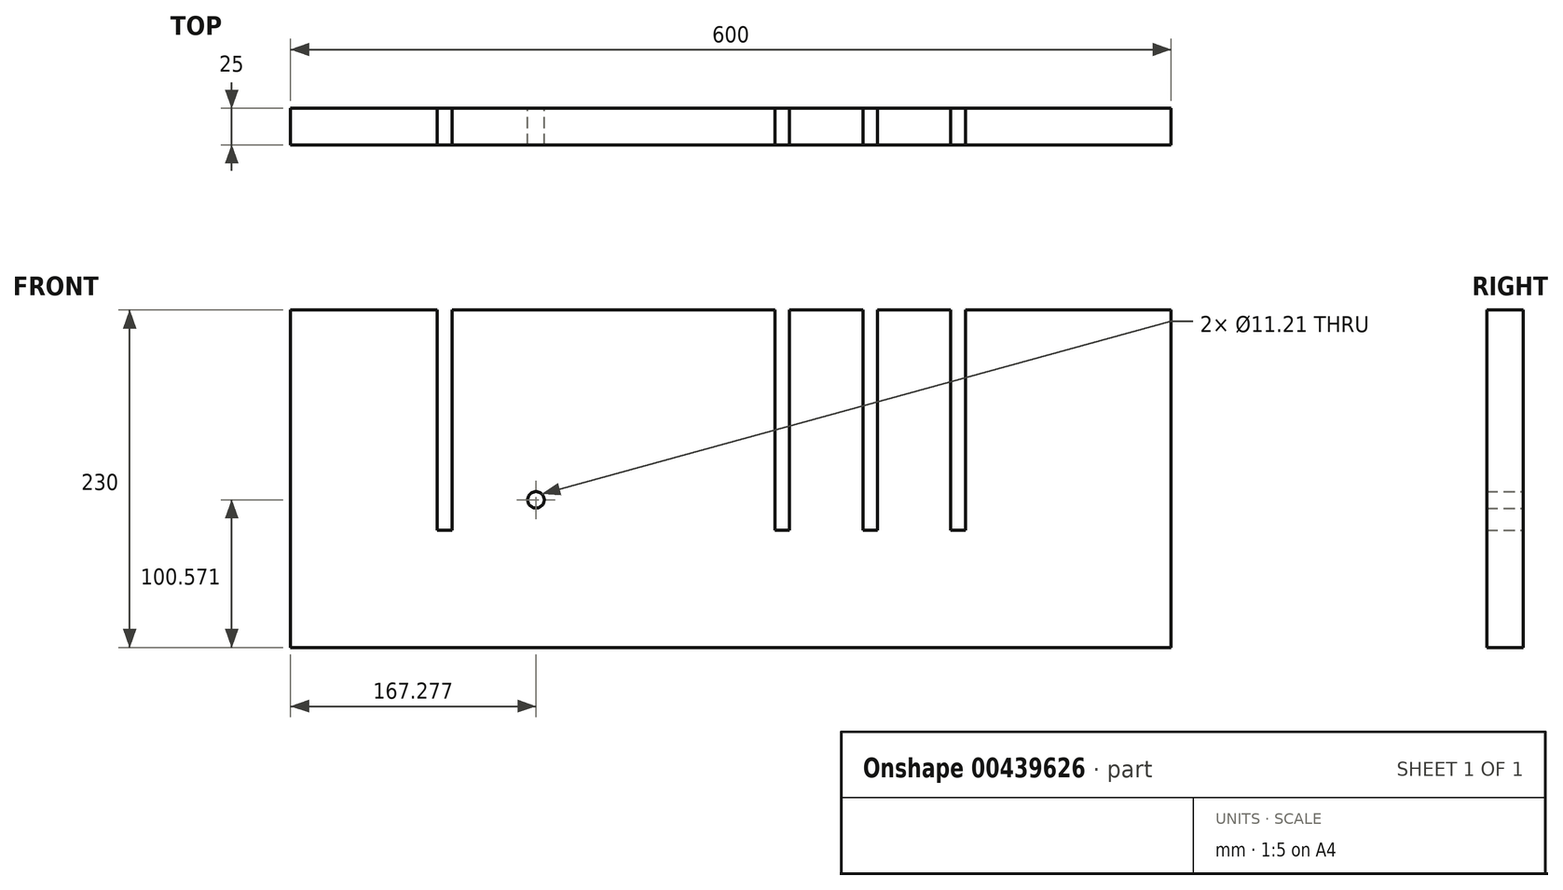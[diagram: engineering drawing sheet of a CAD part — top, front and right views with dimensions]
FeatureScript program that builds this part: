
annotation { "Feature Type Name" : "Feature", "Feature Type Description" : "" }
export const myFeature = defineFeature(function(context is Context, id is Id, definition is map)
    precondition{}
    {
        {
            var Q0;
            Q0=qCreatedBy(makeId("Front.planeOp"),FACE);
            var sketch = newSketch(context, id + "F0", { "sketchPlane" : qUnion([Q0])});
            skLineSegment(sketch, "E0.bottom", {"start": v(-153.84, 195.52) * mm, "end": v(-53.84, 195.52) * mm});
            skLineSegment(sketch, "E0.top", {"start": v(-153.84, -34.48) * mm, "end": v(446.16, -34.48) * mm});
            skLineSegment(sketch, "E0.left", {"start": v(-153.84, 195.52) * mm, "end": v(-153.84, -34.48) * mm});
            skLineSegment(sketch, "E0.right", {"start": v(446.16, 195.52) * mm, "end": v(446.16, -34.48) * mm});
            skLineSegment(sketch, "E1.0", {"start": v(-53.84, 195.52) * mm, "end": v(-53.84, 45.52) * mm});
            skLineSegment(sketch, "E2.0", {"start": v(-43.84, 195.52) * mm, "end": v(-43.84, 45.52) * mm});
            skLineSegment(sketch, "E3.0", {"start": v(176.16, 195.52) * mm, "end": v(176.16, 45.52) * mm});
            skLineSegment(sketch, "E4.0", {"start": v(186.16, 195.52) * mm, "end": v(186.16, 45.52) * mm});
            skLineSegment(sketch, "E5.0", {"start": v(236.16, 195.52) * mm, "end": v(236.16, 45.52) * mm});
            skLineSegment(sketch, "E6.0", {"start": v(246.16, 195.52) * mm, "end": v(246.16, 45.52) * mm});
            skLineSegment(sketch, "E7.0", {"start": v(296.16, 195.52) * mm, "end": v(296.16, 45.52) * mm});
            skLineSegment(sketch, "E8.0", {"start": v(306.16, 195.52) * mm, "end": v(306.16, 45.52) * mm});
            skLineSegment(sketch, "E9.0", {"start": v(-53.84, 45.52) * mm, "end": v(-43.84, 45.52) * mm});
            skLineSegment(sketch, "E10.trimOffspring", {"start": v(176.16, 45.52) * mm, "end": v(186.16, 45.52) * mm});
            skLineSegment(sketch, "E11.trimOffspring", {"start": v(296.16, 45.52) * mm, "end": v(306.16, 45.52) * mm});
            skLineSegment(sketch, "E12", {"start": v(236.16, 45.52) * mm, "end": v(246.16, 45.52) * mm});
            skLineSegment(sketch, "E13.trimOffspring", {"start": v(306.16, 195.52) * mm, "end": v(446.16, 195.52) * mm});
            skLineSegment(sketch, "E14.trimOffspring", {"start": v(246.16, 195.52) * mm, "end": v(296.16, 195.52) * mm});
            skLineSegment(sketch, "E15.trimOffspring", {"start": v(186.16, 195.52) * mm, "end": v(236.16, 195.52) * mm});
            skLineSegment(sketch, "E16.trimOffspring", {"start": v(-43.84, 195.52) * mm, "end": v(176.16, 195.52) * mm});
            skCircle(sketch, "E17", {"center": v(13.44, 66.1) * mm, "radius": 5.6 * mm});
            skSolve(sketch);
        }
        {
            var Q0;
            Q0=makeQuery(id+"F0.imprint","IMPRINT",FACE,{"disambiguationData":[TD([[makeQuery(id+"F0.imprint","IMPRINT",EDGE,{"derivedFrom":sQuery(id+"F0.wireOp",EDGE,"E0.bottom")}),-1.0]])]});
            extrude(context, id + "F1", {"entities" : qUnion([Q0]), "depth" : 25 * mm});
        }
    });
